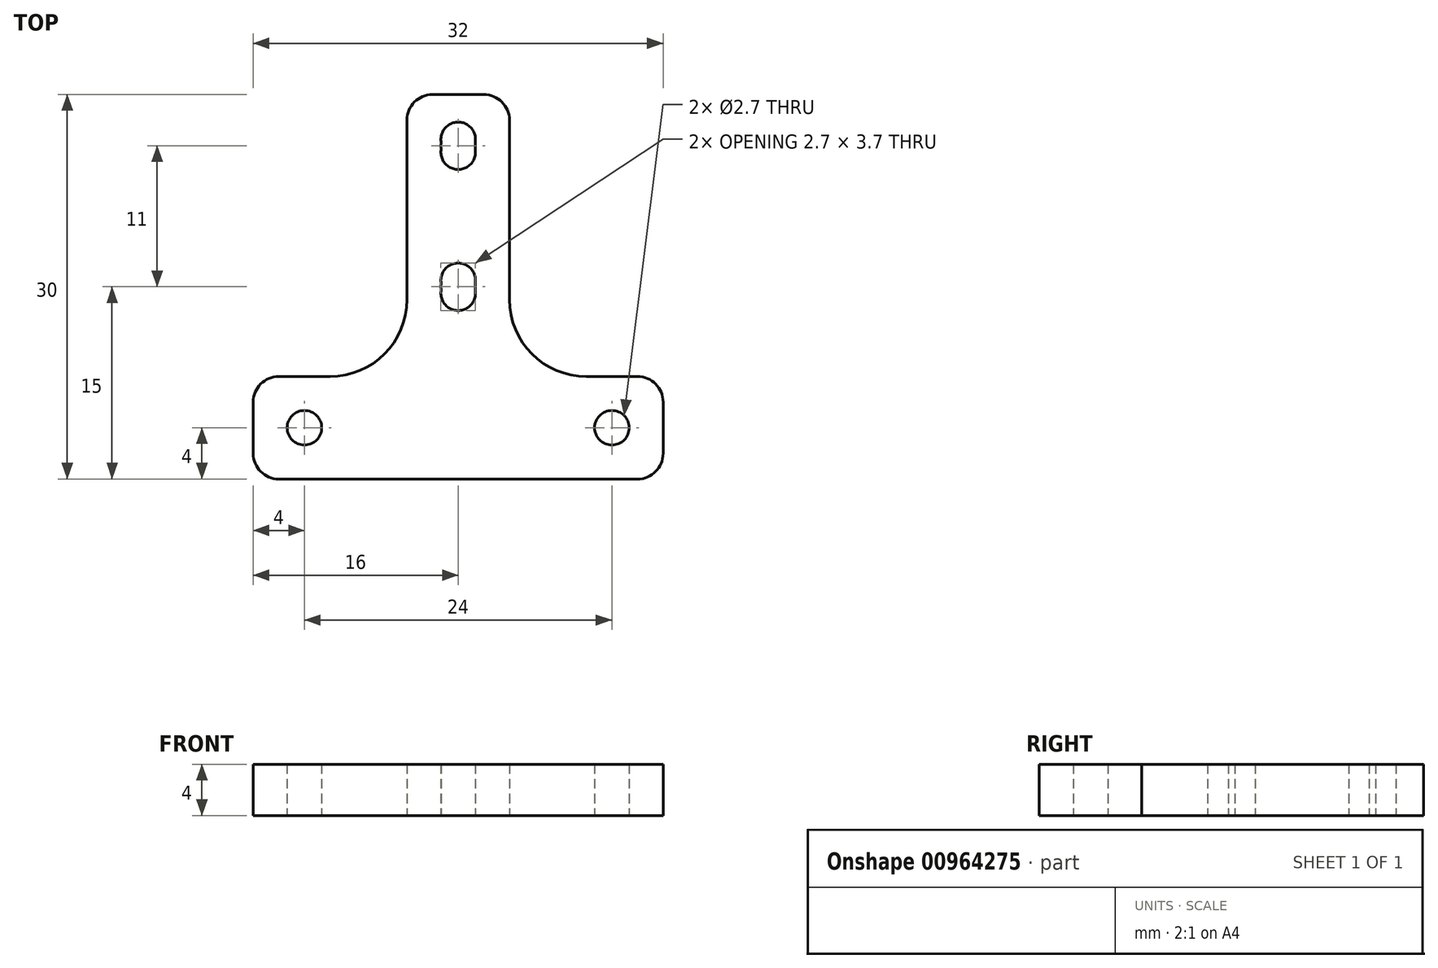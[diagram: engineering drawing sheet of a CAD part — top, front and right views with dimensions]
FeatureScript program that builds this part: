
annotation { "Feature Type Name" : "Feature", "Feature Type Description" : "" }
export const myFeature = defineFeature(function(context is Context, id is Id, definition is map)
    precondition{}
    {
        {
            var Q0;
            Q0=qCreatedBy(makeId("Top.planeOp"),FACE);
            var sketch = newSketch(context, id + "F0", { "sketchPlane" : qUnion([Q0])});
            skLineSegment(sketch, "E0.bottom", {"start": v(4, -15) * mm, "end": v(-4, -15) * mm});
            skLineSegment(sketch, "E0.top", {"start": v(4, 15) * mm, "end": v(-4, 15) * mm});
            skLineSegment(sketch, "E0.left", {"start": v(4, -15) * mm, "end": v(4, 15) * mm});
            skLineSegment(sketch, "E0.right", {"start": v(-4, -15) * mm, "end": v(-4, 15) * mm});
            skPoint(sketch, "E0.middle", {"position": v(0, 0) * mm});
            skLineSegment(sketch, "E1.bottom", {"start": v(4, -15) * mm, "end": v(16, -15) * mm});
            skLineSegment(sketch, "E1.top", {"start": v(4, -7) * mm, "end": v(16, -7) * mm});
            skLineSegment(sketch, "E1.left", {"start": v(4, -15) * mm, "end": v(4, -7) * mm});
            skLineSegment(sketch, "E1.right", {"start": v(16, -15) * mm, "end": v(16, -7) * mm});
            skLineSegment(sketch, "E2.bottom", {"start": v(-4, -15) * mm, "end": v(-16, -15) * mm});
            skLineSegment(sketch, "E2.top", {"start": v(-4, -7) * mm, "end": v(-16, -7) * mm});
            skLineSegment(sketch, "E2.left", {"start": v(-4, -15) * mm, "end": v(-4, -7) * mm});
            skLineSegment(sketch, "E2.right", {"start": v(-16, -15) * mm, "end": v(-16, -7) * mm});
            skPoint(sketch, "E3", {"position": v(0, 11) * mm});
            skPoint(sketch, "E4", {"position": v(-12, -11) * mm});
            skPoint(sketch, "E4.positionSnap0", {"position": v(-4, -11) * mm});
            skPoint(sketch, "E5", {"position": v(12, -11) * mm});
            skPoint(sketch, "E6", {"position": v(0, 10.5) * mm});
            skPoint(sketch, "E7", {"position": v(0, 11.5) * mm});
            skPoint(sketch, "E8", {"position": v(0, -0.5) * mm});
            skPoint(sketch, "E9", {"position": v(0, 0.5) * mm});
            skSolve(sketch);
        }
        {
            var Q0;
            Q0 = qSketchRegion(id + "F0", true);
            extrude(context, id + "F1", {"entities" : qUnion([Q0]), "flatOperationType" : FlatOperationType.REMOVE, "depth" : 4 * mm, "offsetDistance" : 25 * mm, "domain" : OperationDomain.MODEL});
        }
        {
            var Q0;
            Q0=sQuery(id+"F0.wireOp",VERTEX,"E3");
            var Q1;
            Q1=sQuery(id+"F0.wireOp",VERTEX,"E5");
            var Q2;
            Q2=sQuery(id+"F0.wireOp",VERTEX,"E0.middle");
            var Q3;
            Q3=sQuery(id+"F0.wireOp",VERTEX,"E4");
            var Q4;
            Q4=sQuery(id+"F0.wireOp",VERTEX,"E6");
            var Q5;
            Q5=sQuery(id+"F0.wireOp",VERTEX,"E7");
            var Q6;
            Q6=sQuery(id+"F0.wireOp",VERTEX,"E9");
            var Q7;
            Q7=sQuery(id+"F0.wireOp",VERTEX,"E8");
            var Q8;
            Q8=makeQuery(id+"F1.opExtrude","SWEPT_BODY",BODY,{"disambiguationData":[OSD([sQuery(id+"F0.wireOp",EDGE,"E0.bottom"),sQuery(id+"F0.wireOp",EDGE,"E0.top"),sQuery(id+"F0.wireOp",EDGE,"E0.left"),sQuery(id+"F0.wireOp",EDGE,"E0.right"),sQuery(id+"F0.wireOp",EDGE,"E1.bottom"),sQuery(id+"F0.wireOp",EDGE,"E1.top"),sQuery(id+"F0.wireOp",EDGE,"E1.right"),sQuery(id+"F0.wireOp",EDGE,"E2.bottom"),sQuery(id+"F0.wireOp",EDGE,"E2.top"),sQuery(id+"F0.wireOp",EDGE,"E2.right")])]});
            hole(context, id + "F2", {"style" : HoleStyle.SIMPLE, "endStyle" : HoleEndStyle.THROUGH, "oppositeDirection" : true, "holeDiameter" : 2.7 * mm, "majorDiameter" : 5 * mm, "isTappedThrough" : true, "tappedDepth" : 12 * mm, "tapClearance" : 3, "startFromSketch" : true, "locations" : qUnion([Q0, Q1, Q2, Q3, Q4, Q5, Q6, Q7]), "scope" : qUnion([Q8])});
        }
        {
            var Q0;
            Q0=makeQuery(id+"F1.opExtrude","SWEPT_EDGE",EDGE,{"disambiguationData":[OSD([sQuery(id+"F0.wireOp",EDGE,"E0.right"),sQuery(id+"F0.wireOp",EDGE,"E2.top"),sQuery(id+"F0.wireOp",EDGE,"E2.left")])]});
            var Q1;
            Q1=makeQuery(id+"F1.opExtrude","SWEPT_EDGE",EDGE,{"disambiguationData":[OSD([sQuery(id+"F0.wireOp",EDGE,"E0.left"),sQuery(id+"F0.wireOp",EDGE,"E1.top"),sQuery(id+"F0.wireOp",EDGE,"E1.left")])]});
            fillet(context, id + "F3", {"entities" : qUnion([Q0, Q1]), "radius" : 6 * mm, "tangentPropagation" : true, "allowEdgeOverflow" : false});
        }
        {
            var Q0;
            Q0=makeQuery(id+"F1.opExtrude","SWEPT_EDGE",EDGE,{"disambiguationData":[OSD([sQuery(id+"F0.wireOp",EDGE,"E0.top"),sQuery(id+"F0.wireOp",EDGE,"E0.right")])]});
            var Q1;
            Q1=makeQuery(id+"F1.opExtrude","SWEPT_EDGE",EDGE,{"disambiguationData":[OSD([sQuery(id+"F0.wireOp",EDGE,"E0.top"),sQuery(id+"F0.wireOp",EDGE,"E0.left")])]});
            var Q2;
            Q2=makeQuery(id+"F1.opExtrude","SWEPT_EDGE",EDGE,{"disambiguationData":[OSD([sQuery(id+"F0.wireOp",EDGE,"E1.top"),sQuery(id+"F0.wireOp",EDGE,"E1.right")])]});
            var Q3;
            Q3=makeQuery(id+"F1.opExtrude","SWEPT_EDGE",EDGE,{"disambiguationData":[OSD([sQuery(id+"F0.wireOp",EDGE,"E1.bottom"),sQuery(id+"F0.wireOp",EDGE,"E1.right")])]});
            var Q4;
            Q4=makeQuery(id+"F1.opExtrude","SWEPT_EDGE",EDGE,{"disambiguationData":[OSD([sQuery(id+"F0.wireOp",EDGE,"E2.top"),sQuery(id+"F0.wireOp",EDGE,"E2.right")])]});
            var Q5;
            Q5=makeQuery(id+"F1.opExtrude","SWEPT_EDGE",EDGE,{"disambiguationData":[OSD([sQuery(id+"F0.wireOp",EDGE,"E2.bottom"),sQuery(id+"F0.wireOp",EDGE,"E2.right")])]});
            fillet(context, id + "F4", {"entities" : qUnion([Q0, Q1, Q2, Q3, Q4, Q5]), "radius" : 2 * mm, "tangentPropagation" : true, "allowEdgeOverflow" : false});
        }
    });
